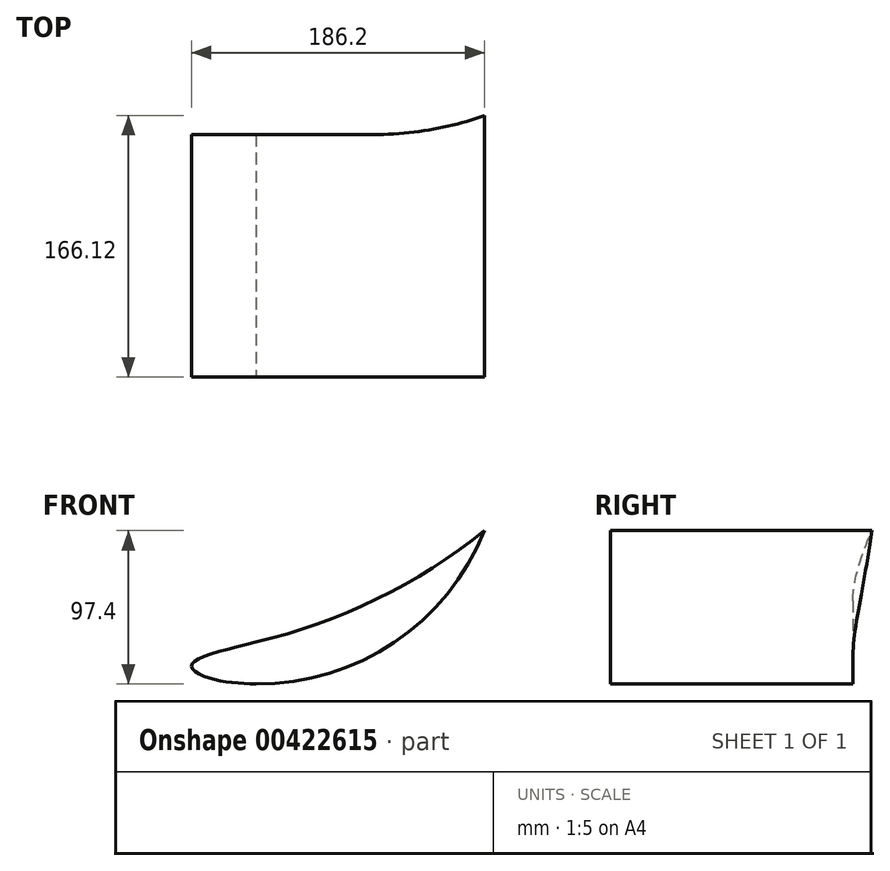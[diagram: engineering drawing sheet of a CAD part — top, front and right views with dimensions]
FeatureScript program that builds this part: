
annotation { "Feature Type Name" : "Feature", "Feature Type Description" : "" }
export const myFeature = defineFeature(function(context is Context, id is Id, definition is map)
    precondition{}
    {
        {
            var Q0;
            Q0=qCreatedBy(makeId("Front.planeOp"),FACE);
            cPlane(context, id + "F0", {"entities" : qUnion([Q0]), "cplaneType" : CPlaneType.OFFSET, "offset" : 509 * mm, "oppositeDirection" : true, "width" : 150 * mm, "height" : 150 * mm});
        }
        {
            var Q0;
            Q0=qCreatedBy(id+"F0.planeOp",FACE);
            var sketch = newSketch(context, id + "F1", { "sketchPlane" : qUnion([Q0])});
            skPoint(sketch, "E0", {"position": v(-847.8, 268.15) * mm});
            skPoint(sketch, "E1", {"position": v(-992.75, 170.76) * mm});
            skPoint(sketch, "E2", {"position": v(-1022.7, 174.47) * mm});
            skPoint(sketch, "E3", {"position": v(-1033.96, 182.47) * mm});
            skPoint(sketch, "E4", {"position": v(-992.75, 197.32) * mm});
            skFitSpline(sketch, "E5", {"points": [v(-992.75, 170.76) * mm, v(-1022.7, 174.47) * mm, v(-1033.96, 182.47) * mm, v(-992.75, 197.32) * mm], "startDerivative": vector(-90, 3.53) * mm, "endDerivative": vector(144.65, 34.4) * mm});
            skArc(sketch, "E6", {"start": v(-992.75, 197.32) * mm, "mid": v(-916.34, 224.7) * mm, "end": v(-847.8, 268.15) * mm});
            skArc(sketch, "E7", {"start": v(-992.75, 170.76) * mm, "mid": v(-905.23, 197.07) * mm, "end": v(-847.8, 268.15) * mm});
            skSolve(sketch);
        }
        {
            var Q0;
            Q0=makeQuery(id+"F1.imprint","IMPRINT",FACE,{"disambiguationData":[TD([[makeQuery(id+"F1.imprint","IMPRINT",EDGE,{"derivedFrom":sQuery(id+"F1.wireOp",EDGE,"E5")}),-1.0]])]});
            extrude(context, id + "F2", {"entities" : qUnion([Q0]), "oppositeDirection" : true, "depth" : 190 * mm});
        }
        {
            var Q0;
            Q0=qCreatedBy(makeId("Top.planeOp"),FACE);
            cPlane(context, id + "F3", {"entities" : qUnion([Q0]), "cplaneType" : CPlaneType.OFFSET, "offset" : 74.53 * mm, "width" : 150 * mm, "height" : 150 * mm});
        }
        {
            var Q0;
            Q0=qCreatedBy(id+"F3.planeOp",FACE);
            var sketch = newSketch(context, id + "F4", { "sketchPlane" : qUnion([Q0])});
            skPoint(sketch, "E8", {"position": v(-1528.3, 663) * mm});
            skPoint(sketch, "E9", {"position": v(-918.77, 663) * mm});
            skPoint(sketch, "E10", {"position": v(-800, 699) * mm});
            skLineSegment(sketch, "E11", {"start": v(-1528.3, 663) * mm, "end": v(-918.77, 663) * mm});
            skArc(sketch, "E12", {"start": v(-918.77, 663) * mm, "mid": v(-856.72, 672.2) * mm, "end": v(-800, 699) * mm});
            skLineSegment(sketch, "E13", {"start": v(-800, 699) * mm, "end": v(-1528.3, 699) * mm});
            skLineSegment(sketch, "E14", {"start": v(-1528.3, 699) * mm, "end": v(-1528.3, 663) * mm});
            skSolve(sketch);
        }
        {
            var Q0;
            Q0=makeQuery(id+"F4.imprint","IMPRINT",FACE,{"disambiguationData":[TD([[makeQuery(id+"F4.imprint","IMPRINT",EDGE,{"derivedFrom":sQuery(id+"F4.wireOp",EDGE,"E11")}),1.0]])]});
            extrude(context, id + "F5", {"entities" : qUnion([Q0]), "operationType" : NewBodyOperationType.REMOVE, "endBound" : BoundingType.THROUGH_ALL, "depth" : 25 * mm});
        }
    });
